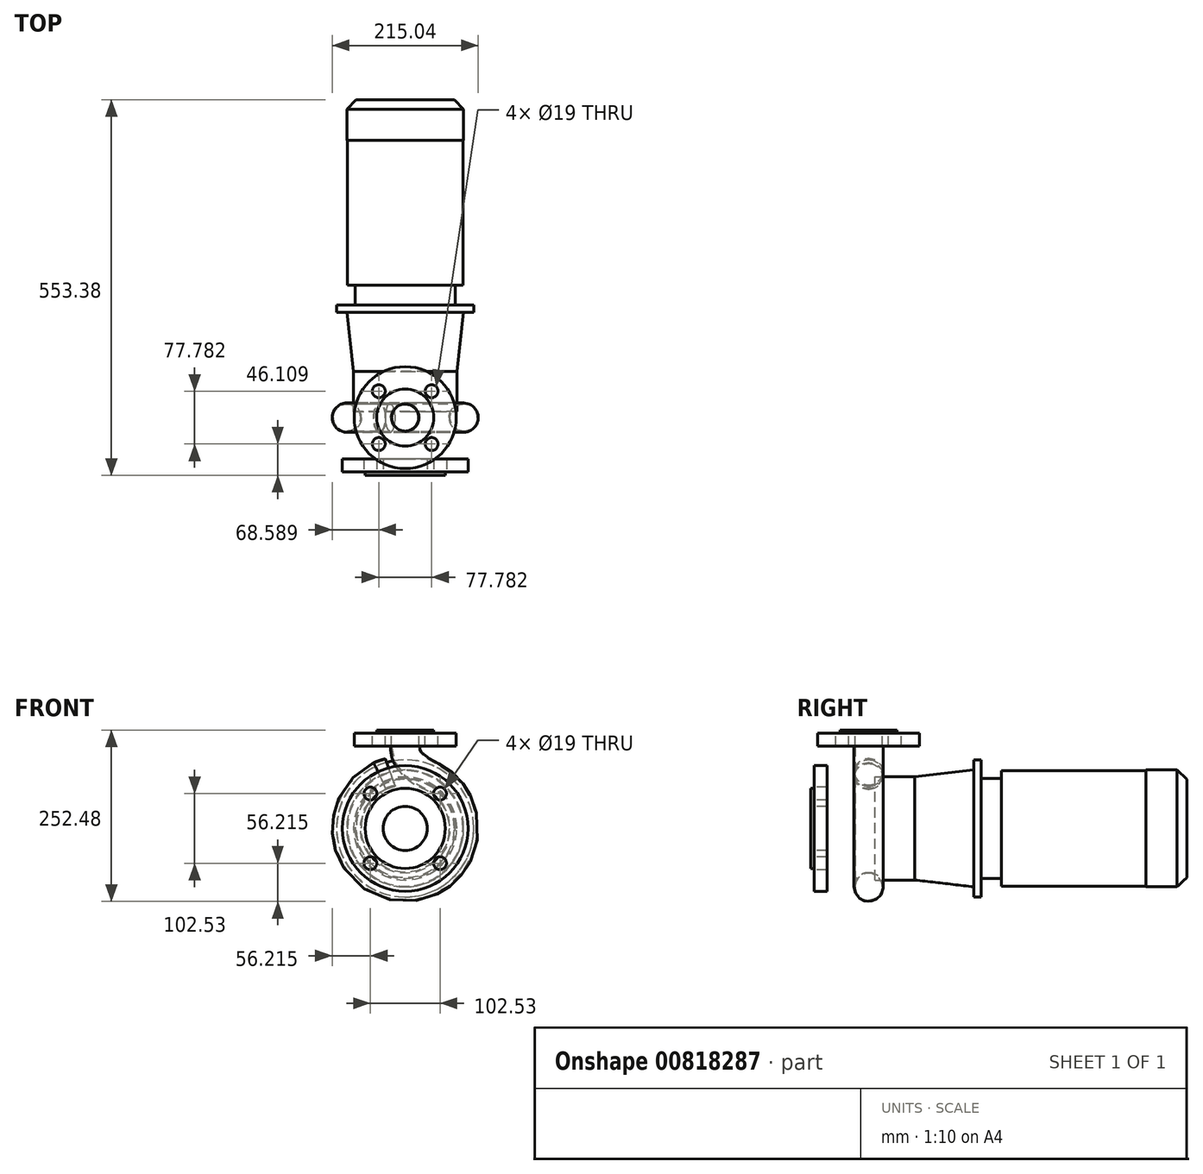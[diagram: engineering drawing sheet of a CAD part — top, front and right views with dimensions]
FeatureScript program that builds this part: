
annotation { "Feature Type Name" : "Feature", "Feature Type Description" : "" }
export const myFeature = defineFeature(function(context is Context, id is Id, definition is map)
    precondition{}
    {
        {
            var Q0;
            Q0=qCreatedBy(makeId("Front.planeOp"),FACE);
            var sketch = newSketch(context, id + "F0", { "sketchPlane" : qUnion([Q0])});
            skCircle(sketch, "E0", {"center": v(0, 0) * mm, "radius": 92.5 * mm});
            skCircle(sketch, "E1", {"center": v(0, 0) * mm, "radius": 32.5 * mm});
            skSolve(sketch);
        }
        {
            var Q0;
            Q0 = qSketchRegion(id + "F0", true);
            extrude(context, id + "F1", {"entities" : qUnion([Q0]), "oppositeDirection" : true, "depth" : 19 * mm, "offsetDistance" : 25 * mm});
        }
        {
            var Q0;
            Q0=makeQuery(id+"F1.opExtrude","CAP_FACE",FACE,{"disambiguationData":[OSD([sQuery(id+"F0.wireOp",EDGE,"E0"),sQuery(id+"F0.wireOp",EDGE,"E1")])],"isStart":true});
            var sketch = newSketch(context, id + "F2", { "sketchPlane" : qUnion([Q0])});
            skCircle(sketch, "E2.0", {"center": v(0, 0) * mm, "radius": 32.5 * mm});
            skCircle(sketch, "E3", {"center": v(0, 0) * mm, "radius": 59 * mm});
            skSolve(sketch);
        }
        {
            var Q0;
            Q0 = qSketchRegion(id + "F2", true);
            extrude(context, id + "F3", {"entities" : qUnion([Q0]), "operationType" : NewBodyOperationType.ADD, "depth" : 5 * mm, "offsetDistance" : 25 * mm});
        }
        {
            var Q0;
            Q0=makeQuery(id+"F1.opExtrude","CAP_FACE",FACE,{"disambiguationData":[OSD([sQuery(id+"F0.wireOp",EDGE,"E0"),sQuery(id+"F0.wireOp",EDGE,"E1")])],"isStart":true});
            var sketch = newSketch(context, id + "F4", { "sketchPlane" : qUnion([Q0])});
            skCircle(sketch, "E4", {"center": v(0, 0) * mm, "radius": 72.5 * mm, "construction": true});
            skLineSegment(sketch, "E5", {"start": v(0, 0) * mm, "end": v(-123.64, 123.64) * mm, "construction": true});
            skCircle(sketch, "E6", {"center": v(-51.27, 51.27) * mm, "radius": 9.5 * mm});
            skCircle(sketch, "E7.1.0", {"center": v(51.27, 51.27) * mm, "radius": 9.5 * mm});
            skCircle(sketch, "E7.2.0", {"center": v(51.27, -51.27) * mm, "radius": 9.5 * mm});
            skLineSegment(sketch, "E7.anchor1", {"start": v(0, 0) * mm, "end": v(-51.27, 51.27) * mm, "construction": true});
            skLineSegment(sketch, "E7.anchor2", {"start": v(0, 0) * mm, "end": v(-51.27, -51.27) * mm, "construction": true});
            skCircle(sketch, "E8.1.3.0", {"center": v(-51.27, -51.27) * mm, "radius": 9.5 * mm});
            skSolve(sketch);
        }
        {
            var Q0;
            Q0 = qSketchRegion(id + "F4", true);
            extrude(context, id + "F5", {"entities" : qUnion([Q0]), "operationType" : NewBodyOperationType.REMOVE, "oppositeDirection" : true, "depth" : 25 * mm, "offsetDistance" : 25 * mm});
        }
        {
            var Q0;
            Q0=qCreatedBy(makeId("Top.planeOp"),FACE);
            cPlane(context, id + "F6", {"entities" : qUnion([Q0]), "cplaneType" : CPlaneType.OFFSET, "offset" : 140 * mm, "width" : 150 * mm, "height" : 150 * mm});
        }
        {
            var Q0;
            Q0=qCreatedBy(id+"F6.planeOp",FACE);
            var sketch = newSketch(context, id + "F7", { "sketchPlane" : qUnion([Q0])});
            skLineSegment(sketch, "E9", {"start": v(0, 0) * mm, "end": v(0, 80) * mm, "construction": true});
            skCircle(sketch, "E10", {"center": v(0, 80) * mm, "radius": 75 * mm});
            skCircle(sketch, "E11", {"center": v(0, 80) * mm, "radius": 20 * mm});
            skSolve(sketch);
        }
        {
            var Q0;
            Q0 = qSketchRegion(id + "F7", true);
            extrude(context, id + "F8", {"entities" : qUnion([Q0]), "oppositeDirection" : true, "depth" : 19 * mm, "offsetDistance" : 25 * mm});
        }
        {
            var Q0;
            Q0=makeQuery(id+"F8.opExtrude","CAP_FACE",FACE,{"disambiguationData":[OSD([sQuery(id+"F7.wireOp",EDGE,"E10"),sQuery(id+"F7.wireOp",EDGE,"E11")])],"isStart":true});
            var sketch = newSketch(context, id + "F9", { "sketchPlane" : qUnion([Q0])});
            skCircle(sketch, "E12.0", {"center": v(0, 80) * mm, "radius": 20 * mm});
            skCircle(sketch, "E13", {"center": v(0, 80) * mm, "radius": 42 * mm});
            skSolve(sketch);
        }
        {
            var Q0;
            Q0 = qSketchRegion(id + "F9", true);
            extrude(context, id + "F10", {"entities" : qUnion([Q0]), "operationType" : NewBodyOperationType.ADD, "depth" : 5 * mm, "offsetDistance" : 25 * mm});
        }
        {
            var Q0;
            Q0=makeQuery(id+"F8.opExtrude","CAP_FACE",FACE,{"disambiguationData":[OSD([sQuery(id+"F7.wireOp",EDGE,"E10"),sQuery(id+"F7.wireOp",EDGE,"E11")])],"isStart":true});
            var sketch = newSketch(context, id + "F11", { "sketchPlane" : qUnion([Q0])});
            skCircle(sketch, "E14.0", {"center": v(0, 80) * mm, "radius": 20 * mm, "construction": true});
            skCircle(sketch, "E15", {"center": v(0, 80) * mm, "radius": 55 * mm, "construction": true});
            skLineSegment(sketch, "E16", {"start": v(0, 80) * mm, "end": v(-110.34, -30.34) * mm, "construction": true});
            skCircle(sketch, "E17", {"center": v(-38.9, 41.1) * mm, "radius": 9.5 * mm});
            skLineSegment(sketch, "E18.1.0", {"start": v(0, 80) * mm, "end": v(110.34, -30.34) * mm, "construction": true});
            skCircle(sketch, "E18.1.1", {"center": v(38.9, 41.1) * mm, "radius": 9.5 * mm});
            skLineSegment(sketch, "E18.2.0", {"start": v(0, 80) * mm, "end": v(110.34, 190.34) * mm, "construction": true});
            skCircle(sketch, "E18.2.1", {"center": v(38.9, 118.9) * mm, "radius": 9.5 * mm});
            skLineSegment(sketch, "E18.3.0", {"start": v(0, 80) * mm, "end": v(-110.34, 190.34) * mm, "construction": true});
            skCircle(sketch, "E18.3.1", {"center": v(-38.9, 118.9) * mm, "radius": 9.5 * mm});
            skSolve(sketch);
        }
        {
            var Q0;
            Q0 = qSketchRegion(id + "F11", true);
            extrude(context, id + "F12", {"entities" : qUnion([Q0]), "operationType" : NewBodyOperationType.REMOVE, "oppositeDirection" : true, "depth" : 25 * mm, "offsetDistance" : 25 * mm});
        }
        {
            var Q0;
            Q0=qCreatedBy(makeId("Front.planeOp"),FACE);
            cPlane(context, id + "F13", {"entities" : qUnion([Q0]), "cplaneType" : CPlaneType.OFFSET, "offset" : 533.8 * mm, "oppositeDirection" : true, "width" : 150 * mm, "height" : 150 * mm});
        }
        {
            var Q0;
            Q0=qCreatedBy(id+"F13.planeOp",FACE);
            var sketch = newSketch(context, id + "F14", { "sketchPlane" : qUnion([Q0])});
            skCircle(sketch, "E19", {"center": v(0, 0) * mm, "radius": 86 * mm});
            skSolve(sketch);
        }
        {
            var Q0;
            Q0 = qSketchRegion(id + "F14", true);
            extrude(context, id + "F15", {"entities" : qUnion([Q0]), "depth" : 45.6 * mm, "offsetDistance" : 25 * mm});
        }
        {
            var Q0;
            Q0=qCreatedBy(id+"F13.planeOp",FACE);
            cPlane(context, id + "F16", {"entities" : qUnion([Q0]), "cplaneType" : CPlaneType.OFFSET, "offset" : 14.58 * mm, "oppositeDirection" : true, "width" : 150 * mm, "height" : 150 * mm});
        }
        {
            var Q0;
            Q0=qCreatedBy(id+"F16.planeOp",FACE);
            var sketch = newSketch(context, id + "F17", { "sketchPlane" : qUnion([Q0])});
            skCircle(sketch, "E20", {"center": v(0, 0) * mm, "radius": 72.32 * mm});
            skCircle(sketch, "E21.0", {"center": v(0, 0) * mm, "radius": 86 * mm, "construction": true});
            skSolve(sketch);
        }
        {
            var Q0;
            Q0 = qSketchRegion(id + "F17", true);
            extrude(context, id + "F18", {"entities" : qUnion([Q0]), "operationType" : NewBodyOperationType.ADD, "depth" : 15 * mm, "offsetDistance" : 25 * mm});
        }
        {
            var Q0;
            Q0=qCreatedBy(makeId("Right.planeOp"),FACE);
            var sketch = newSketch(context, id + "F19", { "sketchPlane" : qUnion([Q0])});
            skLineSegment(sketch, "E22", {"start": v(533.8, 72.32) * mm, "end": v(548.38, 72.32) * mm});
            skLineSegment(sketch, "E23", {"start": v(533.8, 86) * mm, "end": v(548.38, 72.32) * mm});
            skLineSegment(sketch, "E24", {"start": v(533.8, 86) * mm, "end": v(533.8, 72.32) * mm});
            skLineSegment(sketch, "E25", {"start": v(533.8, 0) * mm, "end": v(488.18, 0) * mm, "construction": true});
            skSolve(sketch);
        }
        {
            var Q0;
            Q0 = qSketchRegion(id + "F19", true);
            var Q1;
            Q1=sQuery(id+"F19.wireOp",EDGE,"E25");
            revolve(context, id + "F20", {"operationType" : NewBodyOperationType.ADD, "surfaceOperationType" : NewSurfaceOperationType.NEW, "entities" : qUnion([Q0]), "axis" : qUnion([Q1]), "revolveType" : RevolveType.FULL});
        }
        {
            var Q0;
            Q0=makeQuery(id+"F15.opExtrude","CAP_FACE",FACE,{"disambiguationData":[OSD([sQuery(id+"F14.wireOp",EDGE,"E19")])],"isStart":false});
            var sketch = newSketch(context, id + "F21", { "sketchPlane" : qUnion([Q0])});
            skCircle(sketch, "E26", {"center": v(0, 0) * mm, "radius": 85 * mm});
            skSolve(sketch);
        }
        {
            var Q0;
            Q0 = qSketchRegion(id + "F21", true);
            extrude(context, id + "F22", {"entities" : qUnion([Q0]), "depth" : 212.86 * mm, "offsetDistance" : 25 * mm});
        }
        {
            var Q0;
            Q0=makeQuery(id+"F22.opExtrude","CAP_FACE",FACE,{"disambiguationData":[OSD([sQuery(id+"F21.wireOp",EDGE,"E26")])],"isStart":false});
            var sketch = newSketch(context, id + "F23", { "sketchPlane" : qUnion([Q0])});
            skCircle(sketch, "E27", {"center": v(0, 0) * mm, "radius": 73.78 * mm});
            skSolve(sketch);
        }
        {
            var Q0;
            Q0 = qSketchRegion(id + "F23", true);
            extrude(context, id + "F24", {"entities" : qUnion([Q0]), "depth" : 29.32 * mm, "offsetDistance" : 25 * mm});
        }
        {
            var Q0;
            Q0=makeQuery(id+"F24.opExtrude","CAP_FACE",FACE,{"disambiguationData":[OSD([sQuery(id+"F23.wireOp",EDGE,"E27")])],"isStart":false});
            var sketch = newSketch(context, id + "F25", { "sketchPlane" : qUnion([Q0])});
            skCircle(sketch, "E28", {"center": v(0, 0) * mm, "radius": 93.11 * mm});
            skSolve(sketch);
        }
        {
            var Q0;
            Q0 = qSketchRegion(id + "F25", true);
            extrude(context, id + "F26", {"entities" : qUnion([Q0]), "depth" : 97 * mm, "offsetDistance" : 25 * mm});
        }
        {
            var Q0;
            Q0=qCreatedBy(makeId("Right.planeOp"),FACE);
            var sketch = newSketch(context, id + "F27", { "sketchPlane" : qUnion([Q0])});
            skLineSegment(sketch, "E29", {"start": v(149, 93.11) * mm, "end": v(246, 93.11) * mm});
            skLineSegment(sketch, "E30", {"start": v(246, 93.11) * mm, "end": v(246, 102.11) * mm});
            skLineSegment(sketch, "E31", {"start": v(246, 102.11) * mm, "end": v(149, 93.11) * mm});
            skLineSegment(sketch, "E32", {"start": v(149.37, 0) * mm, "end": v(228.78, 0) * mm, "construction": true});
            skSolve(sketch);
        }
        {
            var Q0;
            Q0 = qSketchRegion(id + "F27", true);
            var Q1;
            Q1=sQuery(id+"F27.wireOp",EDGE,"E32");
            revolve(context, id + "F28", {"operationType" : NewBodyOperationType.ADD, "surfaceOperationType" : NewSurfaceOperationType.NEW, "entities" : qUnion([Q0]), "axis" : qUnion([Q1]), "revolveType" : RevolveType.FULL});
        }
        {
            var Q0;
            Q0=makeQuery(id+"F26.opExtrude","SWEPT_BODY",BODY,{"disambiguationData":[OSD([sQuery(id+"F25.wireOp",EDGE,"E28")])]});
            deleteBodies(context, id + "F29", {"entities" : qUnion([Q0])});
        }
        {
            var Q0;
            Q0=makeQuery(id+"F24.opExtrude","CAP_FACE",FACE,{"disambiguationData":[OSD([sQuery(id+"F23.wireOp",EDGE,"E27")])],"isStart":false});
            var sketch = newSketch(context, id + "F30", { "sketchPlane" : qUnion([Q0])});
            skCircle(sketch, "E33", {"center": v(0, 0) * mm, "radius": 101 * mm});
            skSolve(sketch);
        }
        {
            var Q0;
            Q0 = qSketchRegion(id + "F30", true);
            extrude(context, id + "F31", {"entities" : qUnion([Q0]), "depth" : 11.1 * mm, "offsetDistance" : 25 * mm});
        }
        {
            var Q0;
            Q0=qCreatedBy(id+"F16.planeOp",FACE);
            cPlane(context, id + "F32", {"entities" : qUnion([Q0]), "cplaneType" : CPlaneType.OFFSET, "offset" : 400.63 * mm, "width" : 150 * mm, "height" : 150 * mm});
        }
        {
            var Q0;
            Q0=qCreatedBy(id+"F32.planeOp",FACE);
            var sketch = newSketch(context, id + "F33", { "sketchPlane" : qUnion([Q0])});
            skCircle(sketch, "E34", {"center": v(0, 0) * mm, "radius": 76 * mm});
            skSolve(sketch);
        }
        {
            var Q0;
            Q0 = qSketchRegion(id + "F33", true);
            extrude(context, id + "F34", {"entities" : qUnion([Q0]), "endBound" : BoundingType.UP_TO_NEXT, "oppositeDirection" : true, "depth" : 25 * mm, "offsetDistance" : 25 * mm});
        }
        {
            var Q0;
            Q0=qCreatedBy(makeId("Right.planeOp"),FACE);
            var sketch = newSketch(context, id + "F35", { "sketchPlane" : qUnion([Q0])});
            skLineSegment(sketch, "E35", {"start": v(123.14, 0) * mm, "end": v(239.47, 0) * mm, "construction": true});
            skLineSegment(sketch, "E36.0", {"start": v(147.75, -76) * mm, "end": v(147.75, 76) * mm, "construction": true});
            skLineSegment(sketch, "E37", {"start": v(147.75, 76) * mm, "end": v(234.91, 76) * mm, "construction": true});
            skLineSegment(sketch, "E38", {"start": v(234.91, -76) * mm, "end": v(147.75, -76) * mm, "construction": true});
            skLineSegment(sketch, "E39", {"start": v(147.75, 0) * mm, "end": v(147.75, 76) * mm});
            skLineSegment(sketch, "E40.0", {"start": v(234.9, -101) * mm, "end": v(234.9, 101) * mm, "construction": true});
            skLineSegment(sketch, "E41", {"start": v(147.75, 0) * mm, "end": v(234.9, 0) * mm});
            skLineSegment(sketch, "E42", {"start": v(234.9, 0) * mm, "end": v(234.9, 86) * mm});
            skLineSegment(sketch, "E43", {"start": v(234.9, 86) * mm, "end": v(147.75, 76) * mm});
            skSolve(sketch);
        }
        {
            var Q0;
            Q0 = qSketchRegion(id + "F35", true);
            var Q1;
            Q1=sQuery(id+"F35.wireOp",EDGE,"E41");
            revolve(context, id + "F36", {"operationType" : NewBodyOperationType.ADD, "surfaceOperationType" : NewSurfaceOperationType.NEW, "entities" : qUnion([Q0]), "axis" : qUnion([Q1]), "revolveType" : RevolveType.FULL});
        }
        {
            var Q0;
            Q0=makeQuery(id+"F34.opExtrude","CAP_FACE",FACE,{"disambiguationData":[OSD([sQuery(id+"F33.wireOp",EDGE,"E34")])],"isStart":true});
            var sketch = newSketch(context, id + "F37", { "sketchPlane" : qUnion([Q0])});
            skCircle(sketch, "E44.0", {"center": v(0, 0) * mm, "radius": 76 * mm});
            skSolve(sketch);
        }
        {
            var Q0;
            Q0 = qSketchRegion(id + "F37", true);
            extrude(context, id + "F38", {"entities" : qUnion([Q0]), "depth" : 58.5 * mm, "offsetDistance" : 25 * mm});
        }
        {
            var Q0;
            Q0=makeQuery(id+"F38.opExtrude","CAP_FACE",FACE,{"disambiguationData":[OSD([sQuery(id+"F37.wireOp",EDGE,"E44.0")])],"isStart":false});
            cPlane(context, id + "F39", {"entities" : qUnion([Q0]), "cplaneType" : CPlaneType.OFFSET, "offset" : 22.9 * mm, "width" : 150 * mm, "height" : 150 * mm});
        }
        {
            var Q0;
            Q0=makeQuery(id+"F8.opExtrude","CAP_FACE",FACE,{"disambiguationData":[OSD([sQuery(id+"F7.wireOp",EDGE,"E10"),sQuery(id+"F7.wireOp",EDGE,"E11")])],"isStart":false});
            var sketch = newSketch(context, id + "F40", { "sketchPlane" : qUnion([Q0])});
            skCircle(sketch, "E45.0", {"center": v(0, -80) * mm, "radius": 20 * mm});
            skCircle(sketch, "E46", {"center": v(0, -80) * mm, "radius": 21.5 * mm});
            skSolve(sketch);
        }
        {
            var Q0;
            Q0=qCreatedBy(id+"F39.planeOp",FACE);
            var sketch = newSketch(context, id + "F41", { "sketchPlane" : qUnion([Q0])});
            skLineSegment(sketch, "E47.0", {"start": v(21.5, 121) * mm, "end": v(-21.5, 121) * mm, "construction": true});
            skFitSpline(sketch, "E48", {"points": [v(0, 121) * mm, v(1.8, 108.28) * mm, v(9.04, 96.66) * mm, v(22.65, 85.2) * mm, v(45.48, 73) * mm, v(61.15, 60.47) * mm, v(70.78, 48.85) * mm, v(76.72, 38.85) * mm, v(84.62, 15.35) * mm, v(85.99, -1.42) * mm, v(82.85, -23.08) * mm, v(75.99, -40.27) * mm, v(59.7, -61.9) * mm, v(41.23, -75.47) * mm, v(24.04, -82.57) * mm, v(3.4, -85.93) * mm, v(-17.6, -84.18) * mm, v(-36.95, -77.66) * mm, v(-51.16, -69.12) * mm, v(-68.32, -52.23) * mm, v(-82.68, -23.67) * mm, v(-86, 0) * mm, v(-81.78, 26.6) * mm, v(-70.78, 48.84) * mm, v(-53.52, 67.32) * mm, v(-37.38, 77.45) * mm], "startDerivative": vector(-24.98, -358.76) * mm, "endDerivative": vector(415.44, 229) * mm});
            skFitSpline(sketch, "E49", {"points": [v(-37.38, 77.45) * mm, v(-30.76, 79.9) * mm, v(-22.07, 82.5) * mm], "startDerivative": vector(13.6, 5.3) * mm, "endDerivative": vector(16.96, 4.81) * mm});
            skSolve(sketch);
        }
        {
            var Q0;
            Q0 = qSketchRegion(id + "F40", true);
            var Q1;
            Q1=sQuery(id+"F41.wireOp",EDGE,"E48");
            var Q2;
            Q2=sQuery(id+"F41.wireOp",EDGE,"E49");
            sweep(context, id + "F42", {"profiles" : qUnion([Q0]), "path" : qUnion([Q1, Q2])});
        }
    });
